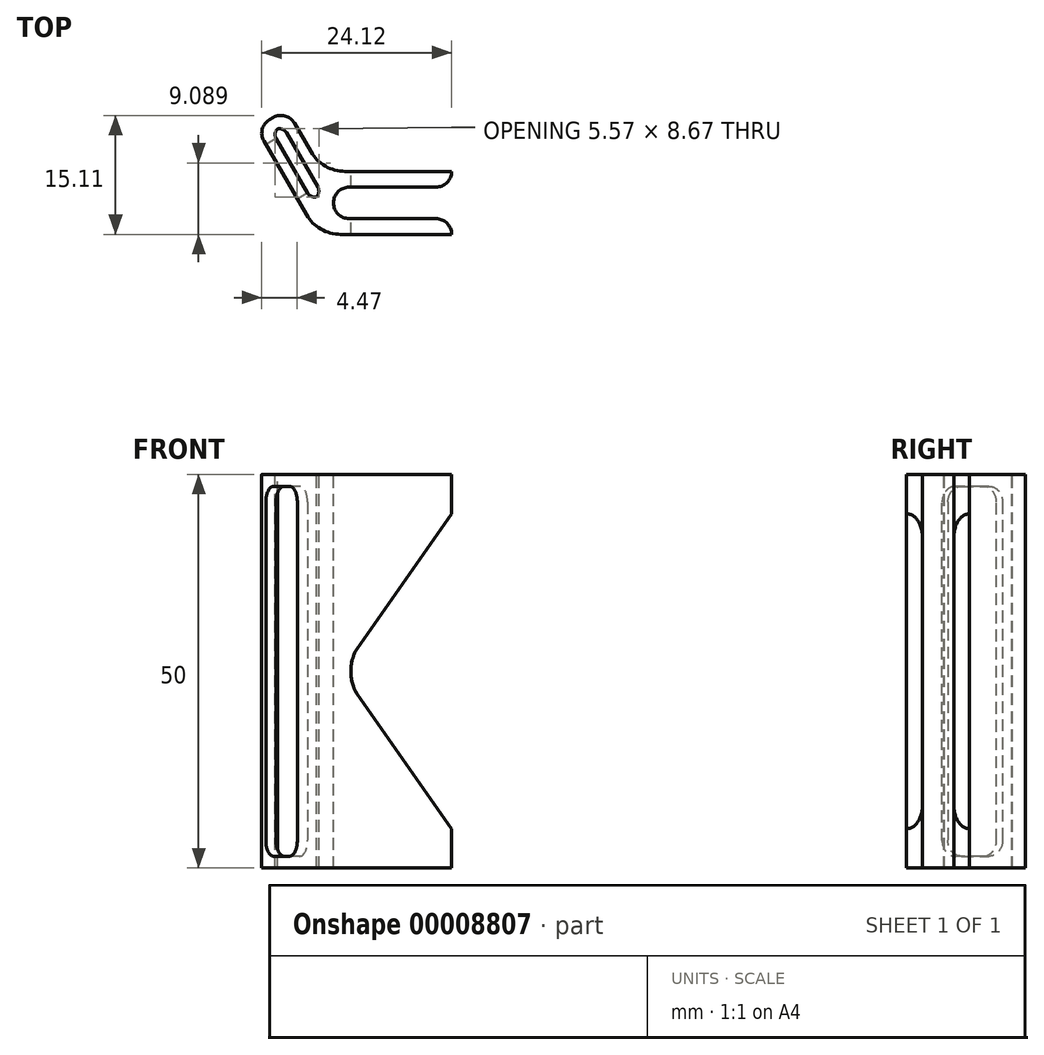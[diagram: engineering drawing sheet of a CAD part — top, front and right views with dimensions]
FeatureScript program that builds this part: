
annotation { "Feature Type Name" : "Feature", "Feature Type Description" : "" }
export const myFeature = defineFeature(function(context is Context, id is Id, definition is map)
    precondition{}
    {
        {
            var Q0;
            Q0=qCreatedBy(makeId("Top.planeOp"),FACE);
            var sketch = newSketch(context, id + "F0", { "sketchPlane" : qUnion([Q0])});
            skLineSegment(sketch, "E0", {"start": v(0, 0) * mm, "end": v(17, 0) * mm});
            skLineSegment(sketch, "E1", {"start": v(17, 0) * mm, "end": v(17, 2) * mm});
            skLineSegment(sketch, "E2", {"start": v(17, 2) * mm, "end": v(2, 2) * mm});
            skLineSegment(sketch, "E3", {"start": v(2, 2) * mm, "end": v(2, 6) * mm});
            skLineSegment(sketch, "E4", {"start": v(2, 6) * mm, "end": v(17, 6) * mm});
            skLineSegment(sketch, "E5", {"start": v(17, 6) * mm, "end": v(17, 8) * mm});
            skLineSegment(sketch, "E6", {"start": v(-7.85, 13.6) * mm, "end": v(0, 0) * mm});
            skLineSegment(sketch, "E7", {"start": v(-7.85, 13.6) * mm, "end": v(-3.95, 15.84) * mm});
            skLineSegment(sketch, "E8", {"start": v(-3.95, 15.84) * mm, "end": v(0.58, 8) * mm});
            skLineSegment(sketch, "E9", {"start": v(-0.8, 4.38) * mm, "end": v(-5.8, 13.04) * mm});
            skLineSegment(sketch, "E10", {"start": v(-5.8, 13.04) * mm, "end": v(-4.5, 13.8) * mm});
            skLineSegment(sketch, "E11", {"start": v(-4.5, 13.8) * mm, "end": v(0.5, 5.13) * mm});
            skLineSegment(sketch, "E12", {"start": v(0.5, 5.13) * mm, "end": v(-0.8, 4.38) * mm});
            skLineSegment(sketch, "E13", {"start": v(17, 8) * mm, "end": v(0.58, 8) * mm});
            skSolve(sketch);
        }
        {
            var Q0;
            Q0=qSketchRegion(id+"F0",true);
            extrude(context, id + "F1", {"entities" : qUnion([Q0]), "depth" : 50 * mm});
        }
        {
            var Q0;
            Q0=makeQuery(id+"F1.opExtrude","SWEPT_EDGE",EDGE,{"disambiguationData":[OSD([sQuery(id+"F0.wireOp",EDGE,"E6"),sQuery(id+"F0.wireOp",EDGE,"E7")])]});
            var Q1;
            Q1=makeQuery(id+"F1.opExtrude","SWEPT_EDGE",EDGE,{"disambiguationData":[OSD([sQuery(id+"F0.wireOp",EDGE,"E2"),sQuery(id+"F0.wireOp",EDGE,"E3")])]});
            var Q2;
            Q2=makeQuery(id+"F1.opExtrude","SWEPT_EDGE",EDGE,{"disambiguationData":[OSD([sQuery(id+"F0.wireOp",EDGE,"E3"),sQuery(id+"F0.wireOp",EDGE,"E4")])]});
            var Q3;
            Q3=makeQuery(id+"F1.opExtrude","SWEPT_EDGE",EDGE,{"disambiguationData":[OSD([sQuery(id+"F0.wireOp",EDGE,"E1"),sQuery(id+"F0.wireOp",EDGE,"E2")])]});
            var Q4;
            Q4=makeQuery(id+"F1.opExtrude","SWEPT_EDGE",EDGE,{"disambiguationData":[OSD([sQuery(id+"F0.wireOp",EDGE,"E4"),sQuery(id+"F0.wireOp",EDGE,"E5")])]});
            var Q5;
            Q5=makeQuery(id+"F1.opExtrude","SWEPT_EDGE",EDGE,{"disambiguationData":[OSD([sQuery(id+"F0.wireOp",EDGE,"E7"),sQuery(id+"F0.wireOp",EDGE,"E8")])]});
            fillet(context, id + "F2", {"entities" : qUnion([Q0, Q1, Q2, Q3, Q4, Q5]), "radius" : 2 * mm, "tangentPropagation" : true, "allowEdgeOverflow" : false});
        }
        {
            var Q0;
            Q0=makeQuery(id+"F1.opExtrude","SWEPT_EDGE",EDGE,{"disambiguationData":[OSD([sQuery(id+"F0.wireOp",EDGE,"E11"),sQuery(id+"F0.wireOp",EDGE,"E12")])]});
            var Q1;
            Q1=makeQuery(id+"F1.opExtrude","SWEPT_EDGE",EDGE,{"disambiguationData":[OSD([sQuery(id+"F0.wireOp",EDGE,"E9"),sQuery(id+"F0.wireOp",EDGE,"E12")])]});
            var Q2;
            Q2=makeQuery(id+"F1.opExtrude","SWEPT_EDGE",EDGE,{"disambiguationData":[OSD([sQuery(id+"F0.wireOp",EDGE,"E9"),sQuery(id+"F0.wireOp",EDGE,"E10")])]});
            var Q3;
            Q3=makeQuery(id+"F1.opExtrude","SWEPT_EDGE",EDGE,{"disambiguationData":[OSD([sQuery(id+"F0.wireOp",EDGE,"E10"),sQuery(id+"F0.wireOp",EDGE,"E11")])]});
            fillet(context, id + "F3", {"entities" : qUnion([Q0, Q1, Q2, Q3]), "radius" : 1 * mm, "tangentPropagation" : true, "allowEdgeOverflow" : false});
        }
        {
            var Q0;
            Q0=makeQuery(id+"F1.opExtrude","SWEPT_FACE",FACE,{"disambiguationData":[OSD([sQuery(id+"F0.wireOp",EDGE,"E6")])]});
            var sketch = newSketch(context, id + "F4", { "sketchPlane" : qUnion([Q0])});
            skLineSegment(sketch, "E14.bottom", {"start": v(-13.2, 1.5) * mm, "end": v(-5.2, 1.5) * mm});
            skLineSegment(sketch, "E14.top", {"start": v(-13.2, 48.5) * mm, "end": v(-5.2, 48.5) * mm});
            skLineSegment(sketch, "E14.left", {"start": v(-13.2, 1.5) * mm, "end": v(-13.2, 48.5) * mm});
            skLineSegment(sketch, "E14.right", {"start": v(-5.2, 1.5) * mm, "end": v(-5.2, 48.5) * mm});
            skSolve(sketch);
        }
        {
            var Q0;
            Q0 = qSketchRegion(id + "F4", true);
            var Q1;
            Q1=makeQuery(id+"F1.opExtrude","SWEPT_FACE",FACE,{"disambiguationData":[OSD([sQuery(id+"F0.wireOp",EDGE,"E9")])]});
            extrude(context, id + "F5", {"entities" : qUnion([Q0]), "operationType" : NewBodyOperationType.REMOVE, "endBound" : BoundingType.UP_TO_SURFACE, "oppositeDirection" : true, "endBoundEntityFace" : qUnion([Q1]), "depth" : 25 * mm});
        }
        {
            var Q0;
            Q0=makeQuery(id+"F5.boolean.opBoolean","COPY",EDGE,{"derivedFrom":makeQuery(id+"F5.opExtrude","SWEPT_EDGE",EDGE,{"disambiguationData":[OSD([sQuery(id+"F4.wireOp",EDGE,"E14.top"),sQuery(id+"F4.wireOp",EDGE,"E14.left")])]})});
            var Q1;
            Q1=makeQuery(id+"F5.boolean.opBoolean","COPY",EDGE,{"derivedFrom":makeQuery(id+"F5.opExtrude","SWEPT_EDGE",EDGE,{"disambiguationData":[OSD([sQuery(id+"F4.wireOp",EDGE,"E14.top"),sQuery(id+"F4.wireOp",EDGE,"E14.right")])]})});
            var Q2;
            Q2=makeQuery(id+"F5.boolean.opBoolean","COPY",EDGE,{"derivedFrom":makeQuery(id+"F5.opExtrude","SWEPT_EDGE",EDGE,{"disambiguationData":[OSD([sQuery(id+"F4.wireOp",EDGE,"E14.bottom"),sQuery(id+"F4.wireOp",EDGE,"E14.right")])]})});
            var Q3;
            Q3=makeQuery(id+"F5.boolean.opBoolean","COPY",EDGE,{"derivedFrom":makeQuery(id+"F5.opExtrude","SWEPT_EDGE",EDGE,{"disambiguationData":[OSD([sQuery(id+"F4.wireOp",EDGE,"E14.bottom"),sQuery(id+"F4.wireOp",EDGE,"E14.left")])]})});
            fillet(context, id + "F6", {"entities" : qUnion([Q0, Q1, Q2, Q3]), "radius" : 2 * mm, "tangentPropagation" : true, "allowEdgeOverflow" : false});
        }
        {
            var Q0;
            Q0=makeQuery(id+"F1.opExtrude","SWEPT_EDGE",EDGE,{"disambiguationData":[OSD([sQuery(id+"F0.wireOp",EDGE,"E8"),sQuery(id+"F0.wireOp",EDGE,"E13")])]});
            var Q1;
            Q1=makeQuery(id+"F1.opExtrude","SWEPT_EDGE",EDGE,{"disambiguationData":[OSD([sQuery(id+"F0.wireOp",EDGE,"E0"),sQuery(id+"F0.wireOp",EDGE,"E6")])]});
            fillet(context, id + "F7", {"entities" : qUnion([Q0, Q1]), "radius" : 5 * mm, "tangentPropagation" : true, "allowEdgeOverflow" : false});
        }
        {
            var Q0;
            Q0=makeQuery(id+"F1.opExtrude","SWEPT_FACE",FACE,{"disambiguationData":[OSD([sQuery(id+"F0.wireOp",EDGE,"E0")])]});
            var sketch = newSketch(context, id + "F8", { "sketchPlane" : qUnion([Q0])});
            skLineSegment(sketch, "E15.bottom", {"start": v(17, 5) * mm, "end": v(3, 25) * mm});
            skLineSegment(sketch, "E15.top", {"start": v(17, 45) * mm, "end": v(3, 25) * mm});
            skLineSegment(sketch, "E15.left", {"start": v(17, 5) * mm, "end": v(17, 45) * mm});
            skSolve(sketch);
        }
        {
            var Q0;
            Q0 = qSketchRegion(id + "F8", true);
            extrude(context, id + "F9", {"entities" : qUnion([Q0]), "operationType" : NewBodyOperationType.REMOVE, "oppositeDirection" : true, "depth" : 25 * mm});
        }
        {
            var Q0;
            Q0=makeQuery(id+"F9.boolean.opBoolean","COPY",EDGE,{"disambiguationData":[OD(0.0)],"derivedFrom":makeQuery(id+"F9.opExtrude","SWEPT_EDGE",EDGE,{"disambiguationData":[OSD([sQuery(id+"F8.wireOp",EDGE,"E15.bottom"),sQuery(id+"F8.wireOp",EDGE,"E15.top")])]})});
            var Q1;
            Q1=makeQuery(id+"F9.boolean.opBoolean","COPY",EDGE,{"disambiguationData":[OD(1.0)],"derivedFrom":makeQuery(id+"F9.opExtrude","SWEPT_EDGE",EDGE,{"disambiguationData":[OSD([sQuery(id+"F8.wireOp",EDGE,"E15.bottom"),sQuery(id+"F8.wireOp",EDGE,"E15.top")])]})});
            fillet(context, id + "F10", {"entities" : qUnion([Q0, Q1]), "radius" : 5 * mm, "tangentPropagation" : true, "rho" : 0.4, "crossSection" : FilletCrossSection.CONIC, "allowEdgeOverflow" : false});
        }
    });
